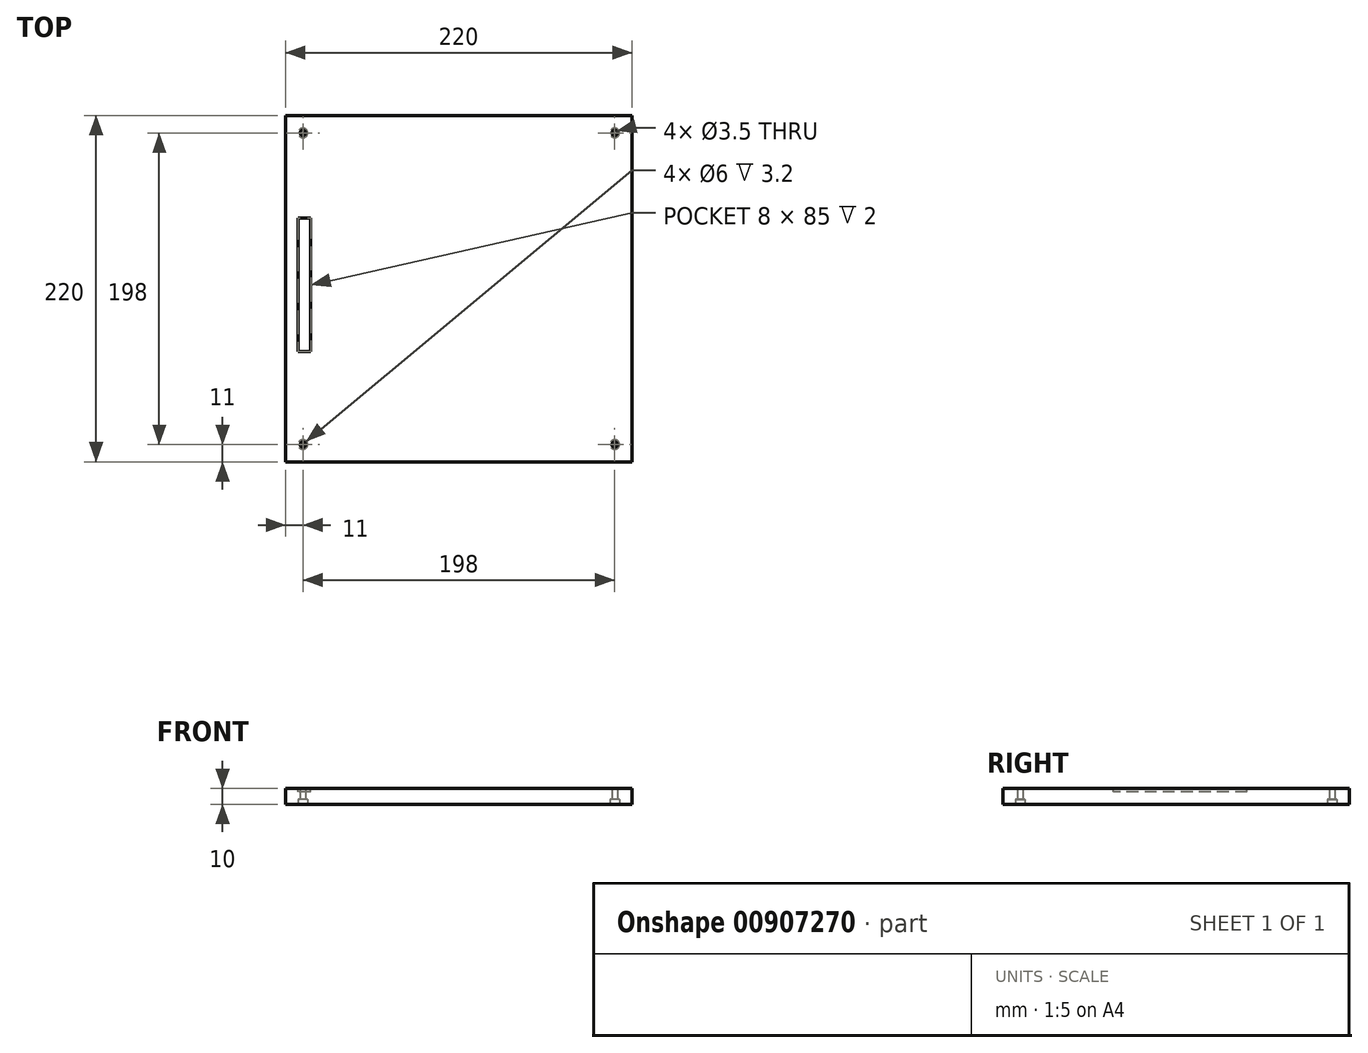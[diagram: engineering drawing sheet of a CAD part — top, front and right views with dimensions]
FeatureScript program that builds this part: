
annotation { "Feature Type Name" : "Feature", "Feature Type Description" : "" }
export const myFeature = defineFeature(function(context is Context, id is Id, definition is map)
    precondition{}
    {
        {
            var Q0;
            Q0=qCreatedBy(makeId("Top.planeOp"),FACE);
            var sketch = newSketch(context, id + "F0", { "sketchPlane" : qUnion([Q0])});
            skLineSegment(sketch, "E0.bottom", {"start": v(110, 110) * mm, "end": v(-110, 110) * mm});
            skLineSegment(sketch, "E0.top", {"start": v(110, -110) * mm, "end": v(-110, -110) * mm});
            skLineSegment(sketch, "E0.left", {"start": v(110, 110) * mm, "end": v(110, -110) * mm});
            skLineSegment(sketch, "E0.right", {"start": v(-110, 110) * mm, "end": v(-110, -110) * mm});
            skPoint(sketch, "E0.middle", {"position": v(0, 0) * mm});
            skLineSegment(sketch, "E1.0", {"start": v(-104, 104) * mm, "end": v(-104, -104) * mm, "construction": true});
            skLineSegment(sketch, "E1.1", {"start": v(104, 104) * mm, "end": v(-104, 104) * mm, "construction": true});
            skLineSegment(sketch, "E1.2", {"start": v(104, 104) * mm, "end": v(104, -104) * mm, "construction": true});
            skLineSegment(sketch, "E1.3", {"start": v(104, -104) * mm, "end": v(-104, -104) * mm, "construction": true});
            skLineSegment(sketch, "E2.0", {"start": v(-99, 99) * mm, "end": v(-99, -99) * mm, "construction": true});
            skLineSegment(sketch, "E2.1", {"start": v(99, 99) * mm, "end": v(-99, 99) * mm, "construction": true});
            skLineSegment(sketch, "E2.2", {"start": v(99, 99) * mm, "end": v(99, -99) * mm, "construction": true});
            skLineSegment(sketch, "E2.3", {"start": v(99, -99) * mm, "end": v(-99, -99) * mm, "construction": true});
            skCircle(sketch, "E3", {"center": v(-99, 99) * mm, "radius": 1.75 * mm});
            skCircle(sketch, "E4", {"center": v(-99, 99) * mm, "radius": 3 * mm});
            skCircle(sketch, "E5.1.0", {"center": v(-99, -99) * mm, "radius": 3 * mm});
            skCircle(sketch, "E5.1.1", {"center": v(-99, -99) * mm, "radius": 1.75 * mm});
            skCircle(sketch, "E5.2.0", {"center": v(99, -99) * mm, "radius": 3 * mm});
            skCircle(sketch, "E5.2.1", {"center": v(99, -99) * mm, "radius": 1.75 * mm});
            skCircle(sketch, "E6.1.3.0", {"center": v(99, 99) * mm, "radius": 3 * mm});
            skCircle(sketch, "E6.2.3.0", {"center": v(99, 99) * mm, "radius": 1.75 * mm});
            skSolve(sketch);
        }
        {
            var Q0;
            Q0=makeQuery(id+"F0.imprint","IMPRINT",FACE,{"disambiguationData":[TD([[makeQuery(id+"F0.imprint","IMPRINT",EDGE,{"derivedFrom":sQuery(id+"F0.wireOp",EDGE,"E0.bottom")}),1.0]])]});
            var Q1;
            Q1=makeQuery(id+"F0.imprint","IMPRINT",FACE,{"disambiguationData":[TD([[makeQuery(id+"F0.imprint","IMPRINT",EDGE,{"derivedFrom":sQuery(id+"F0.wireOp",EDGE,"E3")}),-1.0]])]});
            var Q2;
            Q2=makeQuery(id+"F0.imprint","IMPRINT",FACE,{"disambiguationData":[TD([[makeQuery(id+"F0.imprint","IMPRINT",EDGE,{"derivedFrom":sQuery(id+"F0.wireOp",EDGE,"E6.1.3.0")}),1.0]])]});
            var Q3;
            Q3=makeQuery(id+"F0.imprint","IMPRINT",FACE,{"disambiguationData":[TD([[makeQuery(id+"F0.imprint","IMPRINT",EDGE,{"derivedFrom":sQuery(id+"F0.wireOp",EDGE,"E5.2.0")}),1.0]])]});
            var Q4;
            Q4=makeQuery(id+"F0.imprint","IMPRINT",FACE,{"disambiguationData":[TD([[makeQuery(id+"F0.imprint","IMPRINT",EDGE,{"derivedFrom":sQuery(id+"F0.wireOp",EDGE,"E5.1.0")}),1.0]])]});
            extrude(context, id + "F1", {"entities" : qUnion([Q0, Q1, Q2, Q3, Q4]), "depth" : 10 * mm, "offsetDistance" : 25 * mm});
        }
        {
            var Q0;
            Q0=makeQuery(id+"F0.imprint","IMPRINT",FACE,{"disambiguationData":[TD([[makeQuery(id+"F0.imprint","IMPRINT",EDGE,{"derivedFrom":sQuery(id+"F0.wireOp",EDGE,"E5.1.0")}),1.0]])]});
            var Q1;
            Q1=makeQuery(id+"F0.imprint","IMPRINT",FACE,{"disambiguationData":[TD([[makeQuery(id+"F0.imprint","IMPRINT",EDGE,{"derivedFrom":sQuery(id+"F0.wireOp",EDGE,"E5.2.0")}),1.0]])]});
            var Q2;
            Q2=makeQuery(id+"F0.imprint","IMPRINT",FACE,{"disambiguationData":[TD([[makeQuery(id+"F0.imprint","IMPRINT",EDGE,{"derivedFrom":sQuery(id+"F0.wireOp",EDGE,"E6.1.3.0")}),1.0]])]});
            var Q3;
            Q3=makeQuery(id+"F0.imprint","IMPRINT",FACE,{"disambiguationData":[TD([[makeQuery(id+"F0.imprint","IMPRINT",EDGE,{"derivedFrom":sQuery(id+"F0.wireOp",EDGE,"E3")}),-1.0]])]});
            extrude(context, id + "F2", {"entities" : qUnion([Q0, Q1, Q2, Q3]), "operationType" : NewBodyOperationType.REMOVE, "depth" : 3.2 * mm, "offsetDistance" : 25 * mm});
        }
        {
            var Q0;
            Q0=makeQuery(id+"F1.opExtrude","CAP_FACE",FACE,{"disambiguationData":[OSD([sQuery(id+"F0.wireOp",EDGE,"E0.bottom"),sQuery(id+"F0.wireOp",EDGE,"E0.top"),sQuery(id+"F0.wireOp",EDGE,"E0.left"),sQuery(id+"F0.wireOp",EDGE,"E0.right"),sQuery(id+"F0.wireOp",EDGE,"E3"),sQuery(id+"F0.wireOp",EDGE,"E5.1.1"),sQuery(id+"F0.wireOp",EDGE,"E5.2.1"),sQuery(id+"F0.wireOp",EDGE,"E6.2.3.0")])],"isStart":false});
            var sketch = newSketch(context, id + "F3", { "sketchPlane" : qUnion([Q0])});
            skLineSegment(sketch, "E7.bottom", {"start": v(-94, 45) * mm, "end": v(-102, 45) * mm});
            skLineSegment(sketch, "E7.top", {"start": v(-94, -40) * mm, "end": v(-102, -40) * mm});
            skLineSegment(sketch, "E7.left", {"start": v(-94, 45) * mm, "end": v(-94, -40) * mm});
            skLineSegment(sketch, "E7.right", {"start": v(-102, 45) * mm, "end": v(-102, -40) * mm});
            skSolve(sketch);
        }
        {
            var Q0;
            Q0=makeQuery(id+"F3.imprint","IMPRINT",FACE,{"disambiguationData":[TD([[makeQuery(id+"F3.imprint","IMPRINT",EDGE,{"derivedFrom":sQuery(id+"F3.wireOp",EDGE,"E7.bottom")}),1.0]])]});
            extrude(context, id + "F4", {"entities" : qUnion([Q0]), "operationType" : NewBodyOperationType.REMOVE, "oppositeDirection" : true, "depth" : 2 * mm, "offsetDistance" : 25 * mm});
        }
    });
